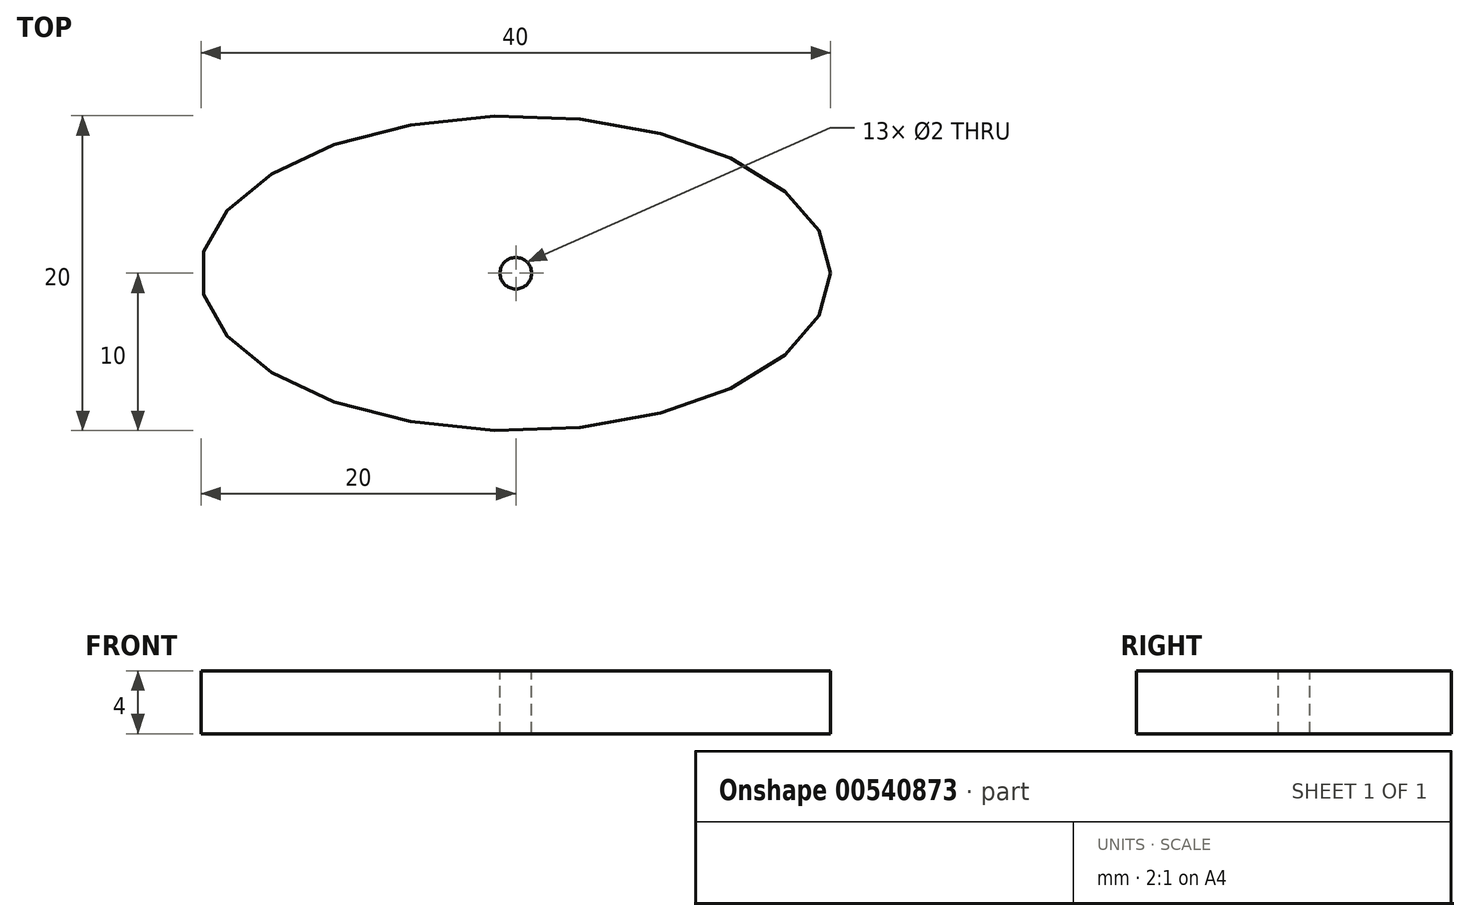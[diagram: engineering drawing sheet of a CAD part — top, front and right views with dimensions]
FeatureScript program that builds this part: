
annotation { "Feature Type Name" : "Feature", "Feature Type Description" : "" }
export const myFeature = defineFeature(function(context is Context, id is Id, definition is map)
    precondition{}
    {
        {
            var Q0;
            Q0=qCreatedBy(makeId("Top.planeOp"),FACE);
            var sketch = newSketch(context, id + "F0", { "sketchPlane" : qUnion([Q0])});
            skLineSegment(sketch, "E0", {"start": v(0, 0) * mm, "end": v(-20, 0) * mm, "construction": true});
            skLineSegment(sketch, "E1.MirrorCS", {"start": v(0, 0) * mm, "end": v(20, 0) * mm, "construction": true});
            skLineSegment(sketch, "E2", {"start": v(0, 0) * mm, "end": v(0, 10) * mm, "construction": true});
            skLineSegment(sketch, "E3.MirrorCS", {"start": v(0, 0) * mm, "end": v(0, -10) * mm, "construction": true});
            skEllipse(sketch, "E4", {"center": v(0, 0) * mm, "majorRadius": 20 * mm, "minorRadius": 10 * mm, "majorAxis": v(1, 0)});
            skSolve(sketch);
        }
        {
            var Q0;
            Q0=makeQuery(id+"F0.imprint","IMPRINT",FACE,{"disambiguationData":[TD([[makeQuery(id+"F0.imprint","IMPRINT",EDGE,{"derivedFrom":sQuery(id+"F0.wireOp",EDGE,"E4")}),1.0]])]});
            extrude(context, id + "F1", {"entities" : qUnion([Q0]), "depth" : 4 * mm, "offsetDistance" : 25 * mm});
        }
        {
            var Q0;
            Q0=makeQuery(id+"F1.opExtrude","CAP_FACE",FACE,{"disambiguationData":[OSD([sQuery(id+"F0.wireOp",EDGE,"E4")])],"isStart":false});
            var sketch = newSketch(context, id + "F2", { "sketchPlane" : qUnion([Q0])});
            skCircle(sketch, "E5", {"center": v(0, 0) * mm, "radius": 1 * mm});
            skSolve(sketch);
        }
        {
            var Q0;
            Q0=makeQuery(id+"F2.imprint","IMPRINT",FACE,{"disambiguationData":[TD([[makeQuery(id+"F2.imprint","IMPRINT",EDGE,{"derivedFrom":sQuery(id+"F2.wireOp",EDGE,"E5")}),1.0]])]});
            extrude(context, id + "F3", {"entities" : qUnion([Q0]), "operationType" : NewBodyOperationType.REMOVE, "oppositeDirection" : true, "depth" : 25 * mm, "offsetDistance" : 25 * mm});
        }
    });
